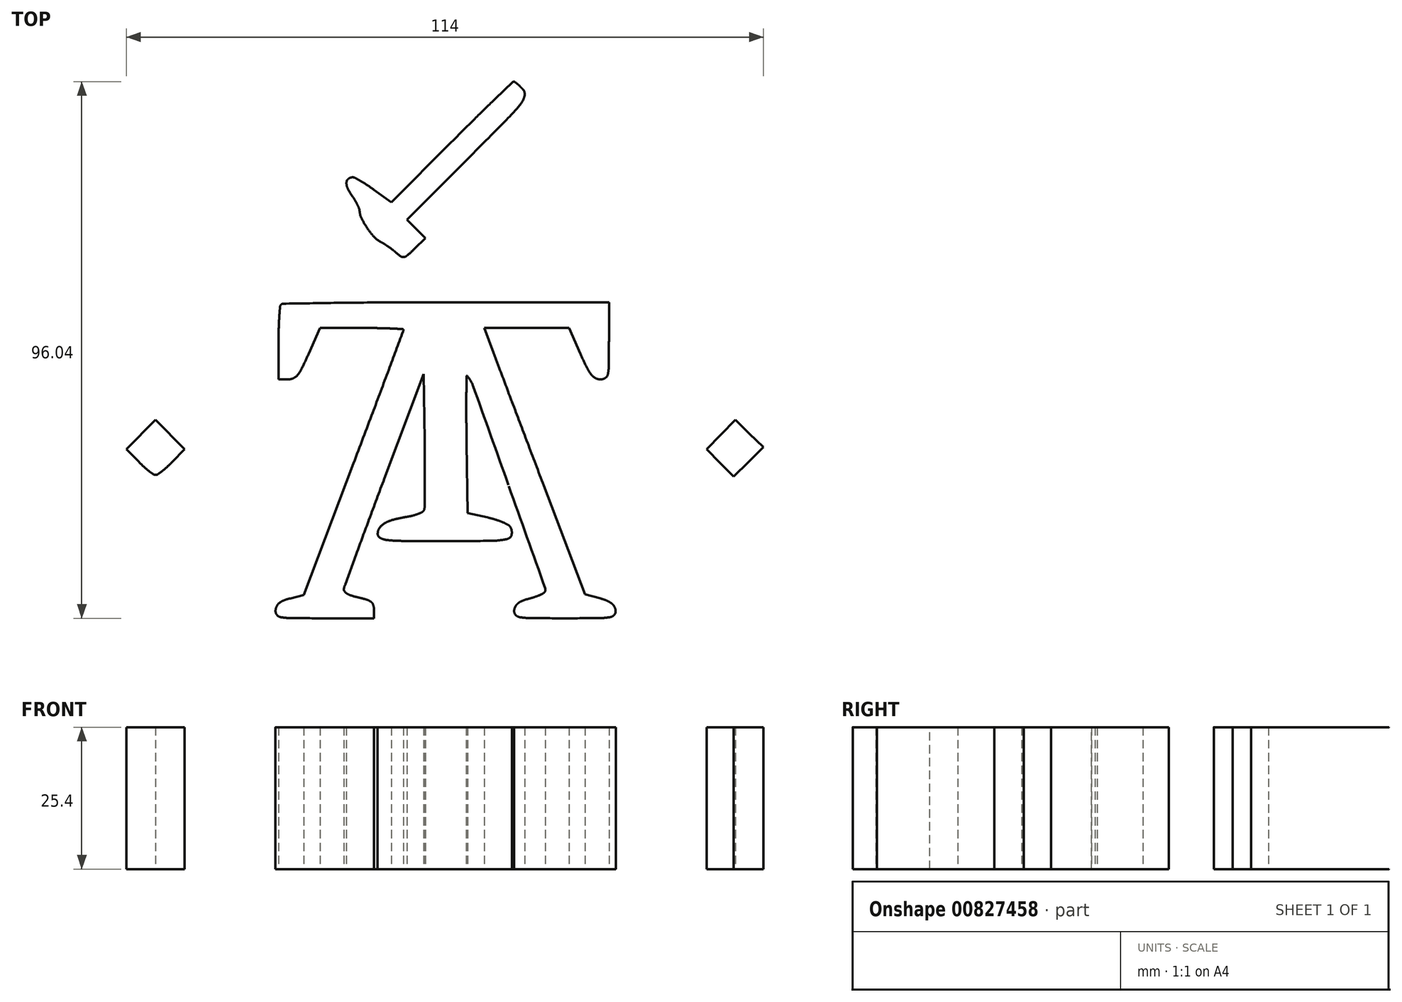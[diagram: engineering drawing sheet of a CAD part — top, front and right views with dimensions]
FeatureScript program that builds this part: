
annotation { "Feature Type Name" : "Feature", "Feature Type Description" : "" }
export const myFeature = defineFeature(function(context is Context, id is Id, definition is map)
    precondition{}
    {
        {
            var Q0;
            Q0=qCreatedBy(makeId("Top.planeOp"),FACE);
            var sketch = newSketch(context, id + "F0", { "sketchPlane" : qUnion([Q0])});
            skLineSegment(sketch, "E0", {"start": v(1.17, 37.24) * mm, "end": v(-9.6, 26.45) * mm});
            skLineSegment(sketch, "E1", {"start": v(-9.6, 26.45) * mm, "end": v(-12.7, 28.68) * mm});
            skArc(sketch, "E2", {"start": v(-12.7, 28.68) * mm, "mid": v(-13.32, 29.12) * mm, "end": v(-13.94, 29.54) * mm});
            skArc(sketch, "E3", {"start": v(-13.94, 29.54) * mm, "mid": v(-14.52, 29.9) * mm, "end": v(-15.1, 30.26) * mm});
            skArc(sketch, "E4", {"start": v(-15.1, 30.26) * mm, "mid": v(-15.6, 30.54) * mm, "end": v(-16.1, 30.81) * mm});
            skArc(sketch, "E5", {"start": v(-16.1, 30.81) * mm, "mid": v(-16.3, 30.9) * mm, "end": v(-16.52, 30.92) * mm});
            skArc(sketch, "E6", {"start": v(-16.52, 30.92) * mm, "mid": v(-16.92, 30.85) * mm, "end": v(-17.29, 30.65) * mm});
            skArc(sketch, "E7", {"start": v(-17.29, 30.65) * mm, "mid": v(-17.53, 30.36) * mm, "end": v(-17.63, 30) * mm});
            skArc(sketch, "E8", {"start": v(-17.63, 30) * mm, "mid": v(-17.59, 29.47) * mm, "end": v(-17.43, 28.97) * mm});
            skArc(sketch, "E9", {"start": v(-17.43, 28.97) * mm, "mid": v(-17.08, 28.31) * mm, "end": v(-16.68, 27.69) * mm});
            skArc(sketch, "E10", {"start": v(-16.68, 27.69) * mm, "mid": v(-16.41, 27.3) * mm, "end": v(-16.16, 26.9) * mm});
            skArc(sketch, "E11", {"start": v(-16.16, 26.9) * mm, "mid": v(-15.93, 26.5) * mm, "end": v(-15.7, 26.08) * mm});
            skArc(sketch, "E12", {"start": v(-15.7, 26.08) * mm, "mid": v(-15.54, 25.72) * mm, "end": v(-15.38, 25.36) * mm});
            skArc(sketch, "E13", {"start": v(-15.38, 25.36) * mm, "mid": v(-15.3, 25.13) * mm, "end": v(-15.28, 24.9) * mm});
            skArc(sketch, "E14", {"start": v(-15.28, 24.9) * mm, "mid": v(-15.17, 24.21) * mm, "end": v(-14.93, 23.56) * mm});
            skArc(sketch, "E15", {"start": v(-14.93, 23.56) * mm, "mid": v(-14.45, 22.67) * mm, "end": v(-13.91, 21.82) * mm});
            skArc(sketch, "E16", {"start": v(-13.91, 21.82) * mm, "mid": v(-13.3, 21) * mm, "end": v(-12.65, 20.22) * mm});
            skArc(sketch, "E17", {"start": v(-12.65, 20.22) * mm, "mid": v(-12.12, 19.73) * mm, "end": v(-11.5, 19.35) * mm});
            skArc(sketch, "E18", {"start": v(-11.5, 19.35) * mm, "mid": v(-11.18, 19.18) * mm, "end": v(-10.86, 18.99) * mm});
            skArc(sketch, "E19", {"start": v(-10.86, 18.99) * mm, "mid": v(-10.48, 18.74) * mm, "end": v(-10.1, 18.49) * mm});
            skArc(sketch, "E20", {"start": v(-10.1, 18.49) * mm, "mid": v(-9.73, 18.22) * mm, "end": v(-9.36, 17.94) * mm});
            skArc(sketch, "E21", {"start": v(-9.36, 17.94) * mm, "mid": v(-9.05, 17.69) * mm, "end": v(-8.75, 17.43) * mm});
            skArc(sketch, "E22", {"start": v(-8.75, 17.43) * mm, "mid": v(-8.33, 17.07) * mm, "end": v(-7.88, 16.75) * mm});
            skArc(sketch, "E23", {"start": v(-7.88, 16.75) * mm, "mid": v(-7.62, 16.64) * mm, "end": v(-7.33, 16.64) * mm});
            skArc(sketch, "E24", {"start": v(-7.33, 16.64) * mm, "mid": v(-7, 16.75) * mm, "end": v(-6.72, 16.94) * mm});
            skArc(sketch, "E25", {"start": v(-6.72, 16.94) * mm, "mid": v(-6.08, 17.52) * mm, "end": v(-5.44, 18.11) * mm});
            skLineSegment(sketch, "E26", {"start": v(-5.44, 18.11) * mm, "end": v(-3.47, 20) * mm});
            skLineSegment(sketch, "E27", {"start": v(-3.47, 20) * mm, "end": v(-5.13, 21.67) * mm});
            skLineSegment(sketch, "E28", {"start": v(-5.13, 21.67) * mm, "end": v(-6.79, 23.33) * mm});
            skLineSegment(sketch, "E29", {"start": v(-6.79, 23.33) * mm, "end": v(4.19, 34.33) * mm});
            skArc(sketch, "E30", {"start": v(4.19, 34.33) * mm, "mid": v(7.8, 37.96) * mm, "end": v(11.39, 41.6) * mm});
            skArc(sketch, "E31", {"start": v(11.39, 41.6) * mm, "mid": v(12.52, 42.81) * mm, "end": v(13.6, 44.09) * mm});
            skArc(sketch, "E32", {"start": v(13.6, 44.09) * mm, "mid": v(14, 44.76) * mm, "end": v(14.26, 45.52) * mm});
            skArc(sketch, "E33", {"start": v(14.26, 45.52) * mm, "mid": v(14.25, 46.14) * mm, "end": v(13.95, 46.68) * mm});
            skArc(sketch, "E34", {"start": v(13.95, 46.68) * mm, "mid": v(13.7, 46.94) * mm, "end": v(13.45, 47.2) * mm});
            skArc(sketch, "E35", {"start": v(13.45, 47.2) * mm, "mid": v(13.22, 47.42) * mm, "end": v(12.97, 47.63) * mm});
            skArc(sketch, "E36", {"start": v(12.97, 47.63) * mm, "mid": v(12.77, 47.8) * mm, "end": v(12.55, 47.95) * mm});
            skArc(sketch, "E37", {"start": v(12.55, 47.95) * mm, "mid": v(12.45, 48) * mm, "end": v(12.33, 48.02) * mm});
            skArc(sketch, "E38", {"start": v(12.33, 48.02) * mm, "mid": v(12.19, 48) * mm, "end": v(12.06, 47.91) * mm});
            skArc(sketch, "E39", {"start": v(12.06, 47.91) * mm, "mid": v(10.48, 46.39) * mm, "end": v(8.9, 44.85) * mm});
            skArc(sketch, "E40", {"start": v(8.9, 44.85) * mm, "mid": v(7.1, 43.12) * mm, "end": v(5.33, 41.37) * mm});
            skArc(sketch, "E41", {"start": v(5.33, 41.37) * mm, "mid": v(3.25, 39.3) * mm, "end": v(1.17, 37.24) * mm});
            skArc(sketch, "E42", {"start": v(-29.35, 8.11) * mm, "mid": v(-29.47, 7.94) * mm, "end": v(-29.52, 7.74) * mm});
            skArc(sketch, "E43", {"start": v(-29.52, 7.74) * mm, "mid": v(-29.6, 6.82) * mm, "end": v(-29.66, 5.9) * mm});
            skArc(sketch, "E44", {"start": v(-29.66, 5.9) * mm, "mid": v(-29.72, 4.81) * mm, "end": v(-29.75, 3.72) * mm});
            skArc(sketch, "E45", {"start": v(-29.75, 3.72) * mm, "mid": v(-29.78, 2.46) * mm, "end": v(-29.79, 1.2) * mm});
            skLineSegment(sketch, "E46", {"start": v(-29.79, 1.2) * mm, "end": v(-29.79, -5.26) * mm});
            skLineSegment(sketch, "E47", {"start": v(-29.79, -5.26) * mm, "end": v(-28.1, -5.26) * mm});
            skArc(sketch, "E48", {"start": v(-28.1, -5.26) * mm, "mid": v(-27.6, -5.2) * mm, "end": v(-27.13, -5.05) * mm});
            skArc(sketch, "E49", {"start": v(-27.13, -5.05) * mm, "mid": v(-26.71, -4.8) * mm, "end": v(-26.36, -4.45) * mm});
            skArc(sketch, "E50", {"start": v(-26.36, -4.45) * mm, "mid": v(-25.94, -3.85) * mm, "end": v(-25.58, -3.21) * mm});
            skArc(sketch, "E51", {"start": v(-25.58, -3.21) * mm, "mid": v(-24.97, -1.94) * mm, "end": v(-24.4, -0.66) * mm});
            skLineSegment(sketch, "E52", {"start": v(-24.4, -0.66) * mm, "end": v(-22.36, 3.95) * mm});
            skLineSegment(sketch, "E53", {"start": v(-22.36, 3.95) * mm, "end": v(-14.9, 3.95) * mm});
            skArc(sketch, "E54", {"start": v(-14.9, 3.95) * mm, "mid": v(-13.47, 3.94) * mm, "end": v(-12.04, 3.92) * mm});
            skArc(sketch, "E55", {"start": v(-12.04, 3.92) * mm, "mid": v(-10.83, 3.9) * mm, "end": v(-9.63, 3.85) * mm});
            skArc(sketch, "E56", {"start": v(-9.63, 3.85) * mm, "mid": v(-8.6, 3.8) * mm, "end": v(-7.57, 3.75) * mm});
            skArc(sketch, "E57", {"start": v(-7.57, 3.74) * mm, "mid": v(-7.48, 3.7) * mm, "end": v(-7.44, 3.6) * mm});
            skArc(sketch, "E58", {"start": v(-7.44, 3.6) * mm, "mid": v(-7.45, 3.47) * mm, "end": v(-7.49, 3.34) * mm});
            skArc(sketch, "E59", {"start": v(-7.49, 3.34) * mm, "mid": v(-8.77, -0.1) * mm, "end": v(-10.06, -3.56) * mm});
            skArc(sketch, "E60", {"start": v(-10.06, -3.56) * mm, "mid": v(-11.5, -7.4) * mm, "end": v(-12.94, -11.24) * mm});
            skArc(sketch, "E61", {"start": v(-12.94, -11.24) * mm, "mid": v(-14.65, -15.77) * mm, "end": v(-16.37, -20.3) * mm});
            skLineSegment(sketch, "E62", {"start": v(-16.37, -20.3) * mm, "end": v(-25.3, -43.87) * mm});
            skLineSegment(sketch, "E63", {"start": v(-25.3, -43.87) * mm, "end": v(-27.7, -44.47) * mm});
            skArc(sketch, "E64", {"start": v(-27.7, -44.47) * mm, "mid": v(-28.29, -44.63) * mm, "end": v(-28.86, -44.83) * mm});
            skArc(sketch, "E65", {"start": v(-28.86, -44.83) * mm, "mid": v(-29.26, -45.02) * mm, "end": v(-29.62, -45.26) * mm});
            skArc(sketch, "E66", {"start": v(-29.62, -45.26) * mm, "mid": v(-29.88, -45.52) * mm, "end": v(-30.09, -45.82) * mm});
            skArc(sketch, "E67", {"start": v(-30.09, -45.82) * mm, "mid": v(-30.24, -46.17) * mm, "end": v(-30.32, -46.54) * mm});
            skArc(sketch, "E68", {"start": v(-30.32, -46.54) * mm, "mid": v(-30.3, -46.98) * mm, "end": v(-30.11, -47.38) * mm});
            skArc(sketch, "E69", {"start": v(-30.11, -47.38) * mm, "mid": v(-29.79, -47.68) * mm, "end": v(-29.38, -47.84) * mm});
            skArc(sketch, "E70", {"start": v(-29.38, -47.84) * mm, "mid": v(-28.46, -47.95) * mm, "end": v(-27.54, -48) * mm});
            skArc(sketch, "E71", {"start": v(-27.54, -48) * mm, "mid": v(-24.58, -48.02) * mm, "end": v(-21.62, -48.02) * mm});
            skLineSegment(sketch, "E72", {"start": v(-21.62, -48.02) * mm, "end": v(-12.7, -48.02) * mm});
            skLineSegment(sketch, "E73", {"start": v(-12.7, -48.02) * mm, "end": v(-12.7, -46.47) * mm});
            skArc(sketch, "E74", {"start": v(-12.7, -46.47) * mm, "mid": v(-12.73, -46.06) * mm, "end": v(-12.83, -45.65) * mm});
            skArc(sketch, "E75", {"start": v(-12.83, -45.65) * mm, "mid": v(-12.99, -45.34) * mm, "end": v(-13.22, -45.1) * mm});
            skArc(sketch, "E76", {"start": v(-13.22, -45.1) * mm, "mid": v(-13.6, -44.86) * mm, "end": v(-14, -44.7) * mm});
            skArc(sketch, "E77", {"start": v(-14, -44.7) * mm, "mid": v(-14.74, -44.48) * mm, "end": v(-15.49, -44.3) * mm});
            skArc(sketch, "E78", {"start": v(-15.49, -44.3) * mm, "mid": v(-16.11, -44.15) * mm, "end": v(-16.73, -43.97) * mm});
            skArc(sketch, "E79", {"start": v(-16.73, -43.97) * mm, "mid": v(-17.15, -43.8) * mm, "end": v(-17.55, -43.6) * mm});
            skArc(sketch, "E80", {"start": v(-17.55, -43.6) * mm, "mid": v(-17.79, -43.41) * mm, "end": v(-17.99, -43.19) * mm});
            skArc(sketch, "E81", {"start": v(-17.99, -43.19) * mm, "mid": v(-18.08, -42.97) * mm, "end": v(-18.08, -42.73) * mm});
            skArc(sketch, "E82", {"start": v(-18.08, -42.73) * mm, "mid": v(-18, -42.36) * mm, "end": v(-17.88, -42) * mm});
            skArc(sketch, "E83", {"start": v(-17.88, -42) * mm, "mid": v(-16.88, -39.28) * mm, "end": v(-15.88, -36.55) * mm});
            skArc(sketch, "E84", {"start": v(-15.88, -36.55) * mm, "mid": v(-14.72, -33.41) * mm, "end": v(-13.56, -30.28) * mm});
            skArc(sketch, "E85", {"start": v(-13.56, -30.28) * mm, "mid": v(-12.2, -26.65) * mm, "end": v(-10.85, -23.03) * mm});
            skLineSegment(sketch, "E86", {"start": v(-10.85, -23.03) * mm, "end": v(-3.82, -4.28) * mm});
            skLineSegment(sketch, "E87", {"start": v(-3.82, -4.28) * mm, "end": v(-3.64, -16.1) * mm});
            skArc(sketch, "E88", {"start": v(-3.64, -16.1) * mm, "mid": v(-3.61, -18.39) * mm, "end": v(-3.6, -20.68) * mm});
            skArc(sketch, "E89", {"start": v(-3.6, -20.68) * mm, "mid": v(-3.6, -22.67) * mm, "end": v(-3.6, -24.66) * mm});
            skArc(sketch, "E90", {"start": v(-3.6, -24.66) * mm, "mid": v(-3.62, -26.37) * mm, "end": v(-3.64, -28.08) * mm});
            skArc(sketch, "E91", {"start": v(-3.64, -28.08) * mm, "mid": v(-3.67, -28.38) * mm, "end": v(-3.75, -28.67) * mm});
            skArc(sketch, "E92", {"start": v(-3.75, -28.67) * mm, "mid": v(-3.86, -28.85) * mm, "end": v(-4.03, -28.98) * mm});
            skArc(sketch, "E93", {"start": v(-4.03, -28.98) * mm, "mid": v(-4.4, -29.17) * mm, "end": v(-4.77, -29.33) * mm});
            skArc(sketch, "E94", {"start": v(-4.77, -29.33) * mm, "mid": v(-5.24, -29.5) * mm, "end": v(-5.73, -29.64) * mm});
            skArc(sketch, "E95", {"start": v(-5.73, -29.64) * mm, "mid": v(-6.26, -29.76) * mm, "end": v(-6.8, -29.86) * mm});
            skArc(sketch, "E96", {"start": v(-6.8, -29.86) * mm, "mid": v(-8.02, -30.08) * mm, "end": v(-9.22, -30.37) * mm});
            skArc(sketch, "E97", {"start": v(-9.22, -30.37) * mm, "mid": v(-10.03, -30.64) * mm, "end": v(-10.8, -31.02) * mm});
            skArc(sketch, "E98", {"start": v(-10.8, -31.02) * mm, "mid": v(-11.3, -31.4) * mm, "end": v(-11.71, -31.86) * mm});
            skArc(sketch, "E99", {"start": v(-11.71, -31.86) * mm, "mid": v(-11.96, -32.37) * mm, "end": v(-12.04, -32.92) * mm});
            skArc(sketch, "E100", {"start": v(-12.04, -32.92) * mm, "mid": v(-11.92, -33.35) * mm, "end": v(-11.6, -33.65) * mm});
            skArc(sketch, "E101", {"start": v(-11.6, -33.65) * mm, "mid": v(-10.98, -33.9) * mm, "end": v(-10.33, -34.03) * mm});
            skArc(sketch, "E102", {"start": v(-10.33, -34.03) * mm, "mid": v(-8.96, -34.14) * mm, "end": v(-7.58, -34.18) * mm});
            skArc(sketch, "E103", {"start": v(-7.58, -34.18) * mm, "mid": v(-3.73, -34.2) * mm, "end": v(0.12, -34.2) * mm});
            skArc(sketch, "E104", {"start": v(0.12, -34.2) * mm, "mid": v(4.26, -34.2) * mm, "end": v(8.4, -34.16) * mm});
            skArc(sketch, "E105", {"start": v(8.4, -34.16) * mm, "mid": v(9.78, -34.07) * mm, "end": v(11.16, -33.84) * mm});
            skArc(sketch, "E106", {"start": v(11.16, -33.84) * mm, "mid": v(11.68, -33.55) * mm, "end": v(11.95, -33.02) * mm});
            skArc(sketch, "E107", {"start": v(11.95, -33.02) * mm, "mid": v(11.95, -32.32) * mm, "end": v(11.7, -31.67) * mm});
            skArc(sketch, "E108", {"start": v(11.7, -31.67) * mm, "mid": v(11.5, -31.44) * mm, "end": v(11.26, -31.27) * mm});
            skArc(sketch, "E109", {"start": v(11.26, -31.27) * mm, "mid": v(10.76, -31.02) * mm, "end": v(10.25, -30.8) * mm});
            skArc(sketch, "E110", {"start": v(10.25, -30.8) * mm, "mid": v(9.62, -30.55) * mm, "end": v(8.99, -30.34) * mm});
            skArc(sketch, "E111", {"start": v(8.99, -30.34) * mm, "mid": v(8.3, -30.14) * mm, "end": v(7.6, -29.97) * mm});
            skLineSegment(sketch, "E112", {"start": v(7.6, -29.97) * mm, "end": v(4.06, -29.18) * mm});
            skLineSegment(sketch, "E113", {"start": v(4.06, -29.18) * mm, "end": v(3.88, -16.77) * mm});
            skArc(sketch, "E114", {"start": v(3.88, -16.77) * mm, "mid": v(3.86, -14.4) * mm, "end": v(3.83, -12.03) * mm});
            skArc(sketch, "E115", {"start": v(3.83, -12.03) * mm, "mid": v(3.83, -10.06) * mm, "end": v(3.84, -8.09) * mm});
            skArc(sketch, "E116", {"start": v(3.84, -8.09) * mm, "mid": v(3.85, -6.39) * mm, "end": v(3.86, -4.69) * mm});
            skArc(sketch, "E117", {"start": v(3.86, -4.69) * mm, "mid": v(3.9, -4.63) * mm, "end": v(3.97, -4.64) * mm});
            skArc(sketch, "E118", {"start": v(3.97, -4.64) * mm, "mid": v(4.58, -5.46) * mm, "end": v(5.02, -6.38) * mm});
            skArc(sketch, "E119", {"start": v(5.02, -6.38) * mm, "mid": v(8.22, -15.33) * mm, "end": v(11.41, -24.28) * mm});
            skArc(sketch, "E120", {"start": v(11.41, -24.28) * mm, "mid": v(14.69, -33.48) * mm, "end": v(17.95, -42.68) * mm});
            skArc(sketch, "E121", {"start": v(17.95, -42.68) * mm, "mid": v(17.97, -43.08) * mm, "end": v(17.77, -43.43) * mm});
            skArc(sketch, "E122", {"start": v(17.77, -43.43) * mm, "mid": v(17.6, -43.57) * mm, "end": v(17.42, -43.67) * mm});
            skArc(sketch, "E123", {"start": v(17.42, -43.67) * mm, "mid": v(17.06, -43.84) * mm, "end": v(16.7, -43.98) * mm});
            skArc(sketch, "E124", {"start": v(16.7, -43.98) * mm, "mid": v(16.27, -44.15) * mm, "end": v(15.83, -44.3) * mm});
            skArc(sketch, "E125", {"start": v(15.83, -44.3) * mm, "mid": v(15.37, -44.43) * mm, "end": v(14.9, -44.56) * mm});
            skArc(sketch, "E126", {"start": v(14.9, -44.56) * mm, "mid": v(14.37, -44.71) * mm, "end": v(13.84, -44.9) * mm});
            skArc(sketch, "E127", {"start": v(13.84, -44.9) * mm, "mid": v(13.45, -45.1) * mm, "end": v(13.1, -45.34) * mm});
            skArc(sketch, "E128", {"start": v(13.1, -45.34) * mm, "mid": v(12.84, -45.6) * mm, "end": v(12.63, -45.9) * mm});
            skArc(sketch, "E129", {"start": v(12.63, -45.9) * mm, "mid": v(12.48, -46.23) * mm, "end": v(12.4, -46.58) * mm});
            skArc(sketch, "E130", {"start": v(12.4, -46.58) * mm, "mid": v(12.43, -47.01) * mm, "end": v(12.63, -47.4) * mm});
            skArc(sketch, "E131", {"start": v(12.63, -47.4) * mm, "mid": v(12.98, -47.69) * mm, "end": v(13.42, -47.84) * mm});
            skArc(sketch, "E132", {"start": v(13.42, -47.84) * mm, "mid": v(14.38, -47.95) * mm, "end": v(15.36, -48) * mm});
            skArc(sketch, "E133", {"start": v(15.36, -48) * mm, "mid": v(18.42, -48.02) * mm, "end": v(21.48, -48.02) * mm});
            skArc(sketch, "E134", {"start": v(21.48, -48.02) * mm, "mid": v(24.53, -48.02) * mm, "end": v(27.58, -48) * mm});
            skArc(sketch, "E135", {"start": v(27.58, -48) * mm, "mid": v(28.56, -47.95) * mm, "end": v(29.53, -47.84) * mm});
            skArc(sketch, "E136", {"start": v(29.53, -47.84) * mm, "mid": v(29.97, -47.69) * mm, "end": v(30.33, -47.4) * mm});
            skArc(sketch, "E137", {"start": v(30.33, -47.4) * mm, "mid": v(30.54, -47.03) * mm, "end": v(30.56, -46.6) * mm});
            skArc(sketch, "E138", {"start": v(30.56, -46.6) * mm, "mid": v(30.47, -46.24) * mm, "end": v(30.31, -45.9) * mm});
            skArc(sketch, "E139", {"start": v(30.31, -45.9) * mm, "mid": v(30.08, -45.6) * mm, "end": v(29.8, -45.33) * mm});
            skArc(sketch, "E140", {"start": v(29.8, -45.33) * mm, "mid": v(29.4, -45.07) * mm, "end": v(28.97, -44.86) * mm});
            skArc(sketch, "E141", {"start": v(28.97, -44.86) * mm, "mid": v(28.35, -44.63) * mm, "end": v(27.73, -44.44) * mm});
            skLineSegment(sketch, "E142", {"start": v(27.73, -44.44) * mm, "end": v(25.1, -43.7) * mm});
            skLineSegment(sketch, "E143", {"start": v(25.1, -43.7) * mm, "end": v(17.72, -24.32) * mm});
            skArc(sketch, "E144", {"start": v(17.72, -24.32) * mm, "mid": v(16.25, -20.45) * mm, "end": v(14.78, -16.57) * mm});
            skArc(sketch, "E145", {"start": v(14.78, -16.57) * mm, "mid": v(13.4, -12.95) * mm, "end": v(12.03, -9.32) * mm});
            skArc(sketch, "E146", {"start": v(12.03, -9.32) * mm, "mid": v(10.88, -6.28) * mm, "end": v(9.72, -3.23) * mm});
            skArc(sketch, "E147", {"start": v(9.72, -3.23) * mm, "mid": v(9.2, -1.86) * mm, "end": v(8.7, -0.5) * mm});
            skLineSegment(sketch, "E148", {"start": v(8.7, -0.5) * mm, "end": v(7.05, 3.95) * mm});
            skLineSegment(sketch, "E149", {"start": v(7.05, 3.95) * mm, "end": v(14.63, 3.95) * mm});
            skLineSegment(sketch, "E150", {"start": v(14.63, 3.95) * mm, "end": v(22.21, 3.95) * mm});
            skLineSegment(sketch, "E151", {"start": v(22.21, 3.95) * mm, "end": v(24.25, -0.66) * mm});
            skArc(sketch, "E152", {"start": v(24.25, -0.66) * mm, "mid": v(24.8, -1.9) * mm, "end": v(25.4, -3.12) * mm});
            skArc(sketch, "E153", {"start": v(25.4, -3.12) * mm, "mid": v(25.76, -3.78) * mm, "end": v(26.19, -4.4) * mm});
            skArc(sketch, "E154", {"start": v(26.19, -4.4) * mm, "mid": v(26.53, -4.75) * mm, "end": v(26.94, -5.03) * mm});
            skArc(sketch, "E155", {"start": v(26.94, -5.03) * mm, "mid": v(27.37, -5.2) * mm, "end": v(27.82, -5.26) * mm});
            skArc(sketch, "E156", {"start": v(27.82, -5.26) * mm, "mid": v(28.28, -5.2) * mm, "end": v(28.7, -5.01) * mm});
            skArc(sketch, "E157", {"start": v(28.7, -5.01) * mm, "mid": v(29, -4.74) * mm, "end": v(29.17, -4.36) * mm});
            skArc(sketch, "E158", {"start": v(29.17, -4.36) * mm, "mid": v(29.3, -3.63) * mm, "end": v(29.34, -2.88) * mm});
            skArc(sketch, "E159", {"start": v(29.34, -2.88) * mm, "mid": v(29.36, -0.62) * mm, "end": v(29.37, 1.64) * mm});
            skLineSegment(sketch, "E160", {"start": v(29.37, 1.64) * mm, "end": v(29.37, 8.55) * mm});
            skLineSegment(sketch, "E161", {"start": v(29.37, 8.55) * mm, "end": v(0.23, 8.55) * mm});
            skArc(sketch, "E162", {"start": v(0.23, 8.55) * mm, "mid": v(-5.37, 8.54) * mm, "end": v(-10.97, 8.52) * mm});
            skArc(sketch, "E163", {"start": v(-10.97, 8.52) * mm, "mid": v(-15.73, 8.48) * mm, "end": v(-20.48, 8.42) * mm});
            skArc(sketch, "E164", {"start": v(-20.48, 8.42) * mm, "mid": v(-24.7, 8.36) * mm, "end": v(-28.92, 8.3) * mm});
            skArc(sketch, "E165", {"start": v(-28.92, 8.3) * mm, "mid": v(-29.15, 8.24) * mm, "end": v(-29.35, 8.11) * mm});
            skLineSegment(sketch, "E166", {"start": v(-54.42, -15.12) * mm, "end": v(-57, -17.76) * mm});
            skLineSegment(sketch, "E167", {"start": v(-57, -17.76) * mm, "end": v(-54.76, -20.06) * mm});
            skArc(sketch, "E168", {"start": v(-54.76, -20.06) * mm, "mid": v(-54.32, -20.51) * mm, "end": v(-53.86, -20.95) * mm});
            skArc(sketch, "E169", {"start": v(-53.86, -20.95) * mm, "mid": v(-53.42, -21.33) * mm, "end": v(-52.97, -21.7) * mm});
            skArc(sketch, "E170", {"start": v(-52.97, -21.7) * mm, "mid": v(-52.6, -21.97) * mm, "end": v(-52.2, -22.24) * mm});
            skArc(sketch, "E171", {"start": v(-52.2, -22.24) * mm, "mid": v(-52.01, -22.34) * mm, "end": v(-51.8, -22.37) * mm});
            skArc(sketch, "E172", {"start": v(-51.8, -22.37) * mm, "mid": v(-51.6, -22.34) * mm, "end": v(-51.4, -22.24) * mm});
            skArc(sketch, "E173", {"start": v(-51.4, -22.24) * mm, "mid": v(-51.01, -21.97) * mm, "end": v(-50.63, -21.69) * mm});
            skArc(sketch, "E174", {"start": v(-50.63, -21.69) * mm, "mid": v(-50.18, -21.32) * mm, "end": v(-49.75, -20.94) * mm});
            skArc(sketch, "E175", {"start": v(-49.75, -20.94) * mm, "mid": v(-49.28, -20.5) * mm, "end": v(-48.83, -20.05) * mm});
            skLineSegment(sketch, "E176", {"start": v(-48.83, -20.05) * mm, "end": v(-46.6, -17.74) * mm});
            skLineSegment(sketch, "E177", {"start": v(-46.6, -17.74) * mm, "end": v(-49.22, -15.1) * mm});
            skLineSegment(sketch, "E178", {"start": v(-49.22, -15.1) * mm, "end": v(-51.84, -12.48) * mm});
            skLineSegment(sketch, "E179", {"start": v(-51.84, -12.48) * mm, "end": v(-54.42, -15.12) * mm});
            skLineSegment(sketch, "E180", {"start": v(49.4, -15.14) * mm, "end": v(46.83, -17.78) * mm});
            skLineSegment(sketch, "E181", {"start": v(46.83, -17.78) * mm, "end": v(49.27, -20.23) * mm});
            skLineSegment(sketch, "E182", {"start": v(49.27, -20.23) * mm, "end": v(51.72, -22.68) * mm});
            skLineSegment(sketch, "E183", {"start": v(51.72, -22.68) * mm, "end": v(54.36, -20.03) * mm});
            skLineSegment(sketch, "E184", {"start": v(54.36, -20.03) * mm, "end": v(57, -17.4) * mm});
            skLineSegment(sketch, "E185", {"start": v(57, -17.4) * mm, "end": v(54.5, -14.94) * mm});
            skLineSegment(sketch, "E186", {"start": v(54.5, -14.94) * mm, "end": v(51.99, -12.5) * mm});
            skLineSegment(sketch, "E187", {"start": v(51.99, -12.5) * mm, "end": v(49.4, -15.14) * mm});
            skSolve(sketch);
        }
        {
            var Q0;
            Q0=makeQuery(id+"F0.imprint","IMPRINT",FACE,{"disambiguationData":[TD([[makeQuery(id+"F0.imprint","IMPRINT",EDGE,{"derivedFrom":sQuery(id+"F0.wireOp",EDGE,"E0")}),1.0]])]});
            var Q1;
            Q1=makeQuery(id+"F0.imprint","IMPRINT",FACE,{"disambiguationData":[TD([[makeQuery(id+"F0.imprint","IMPRINT",EDGE,{"derivedFrom":sQuery(id+"F0.wireOp",EDGE,"E42")}),1.0]])]});
            var Q2;
            Q2=makeQuery(id+"F0.imprint","IMPRINT",FACE,{"disambiguationData":[TD([[makeQuery(id+"F0.imprint","IMPRINT",EDGE,{"derivedFrom":sQuery(id+"F0.wireOp",EDGE,"E166")}),1.0]])]});
            var Q3;
            Q3=makeQuery(id+"F0.imprint","IMPRINT",FACE,{"disambiguationData":[TD([[makeQuery(id+"F0.imprint","IMPRINT",EDGE,{"derivedFrom":sQuery(id+"F0.wireOp",EDGE,"E180")}),1.0]])]});
            extrude(context, id + "F1", {"entities" : qUnion([Q0, Q1, Q2, Q3]), "depth" : 25.4 * mm, "offsetDistance" : 25.4 * mm});
        }
    });
